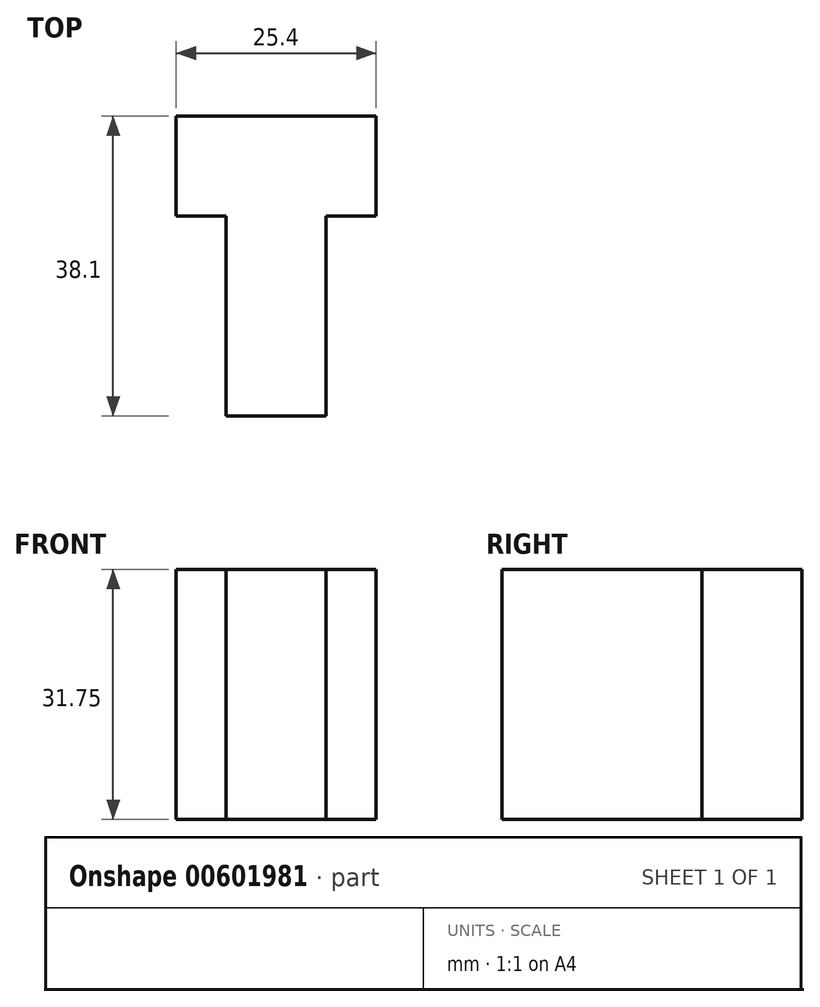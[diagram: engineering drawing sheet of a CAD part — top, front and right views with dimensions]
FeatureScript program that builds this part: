
annotation { "Feature Type Name" : "Feature", "Feature Type Description" : "" }
export const myFeature = defineFeature(function(context is Context, id is Id, definition is map)
    precondition{}
    {
        {
            var Q0;
            Q0=qCreatedBy(makeId("Top.planeOp"),FACE);
            var sketch = newSketch(context, id + "F0", { "sketchPlane" : qUnion([Q0])});
            skLineSegment(sketch, "E0", {"start": v(0, 0) * mm, "end": v(0, -25.4) * mm});
            skLineSegment(sketch, "E1", {"start": v(0, -25.4) * mm, "end": v(12.7, -25.4) * mm});
            skLineSegment(sketch, "E2", {"start": v(12.7, -25.4) * mm, "end": v(12.7, 0) * mm});
            skLineSegment(sketch, "E3", {"start": v(12.7, 0) * mm, "end": v(19.05, 0) * mm});
            skLineSegment(sketch, "E4", {"start": v(19.05, 0) * mm, "end": v(19.05, 12.7) * mm});
            skLineSegment(sketch, "E5", {"start": v(19.05, 12.7) * mm, "end": v(-6.35, 12.7) * mm});
            skLineSegment(sketch, "E6", {"start": v(-6.35, 12.7) * mm, "end": v(-6.35, 0) * mm});
            skLineSegment(sketch, "E7", {"start": v(-6.35, 0) * mm, "end": v(0, 0) * mm});
            skSolve(sketch);
        }
        {
            var Q0;
            Q0=makeQuery(id+"F0.imprint","IMPRINT",FACE,{"disambiguationData":[TD([[makeQuery(id+"F0.imprint","IMPRINT",EDGE,{"derivedFrom":sQuery(id+"F0.wireOp",EDGE,"E0")}),1.0]])]});
            extrude(context, id + "F1", {"entities" : qUnion([Q0]), "depth" : 31.75 * mm, "offsetDistance" : 25.4 * mm});
        }
    });
